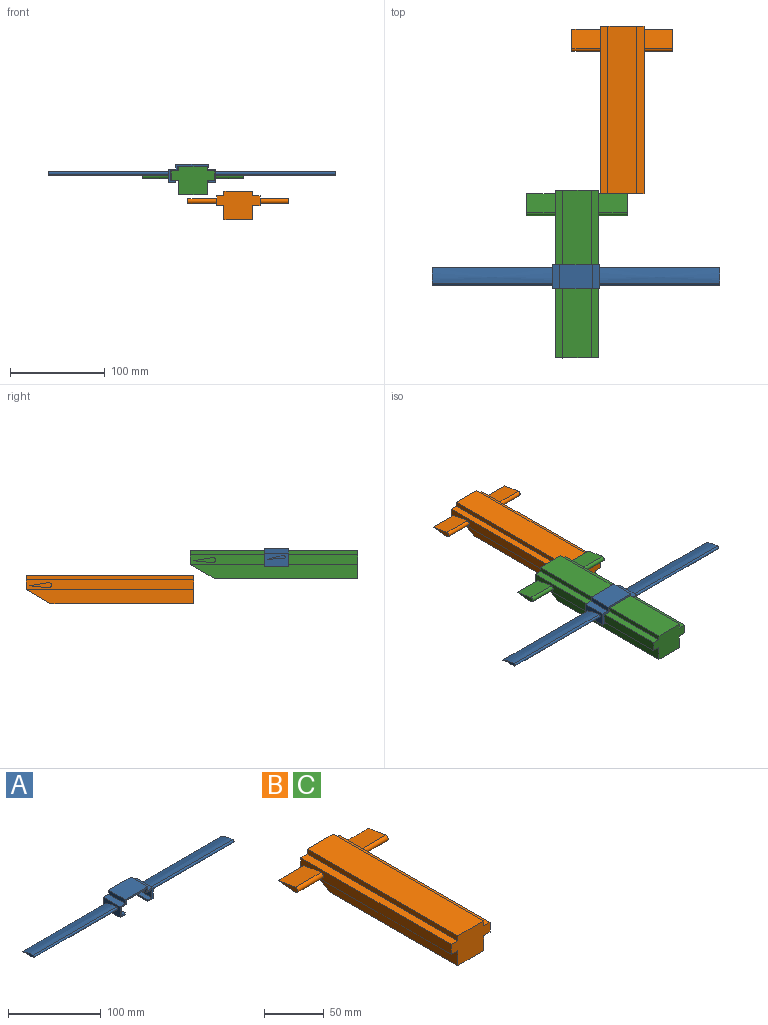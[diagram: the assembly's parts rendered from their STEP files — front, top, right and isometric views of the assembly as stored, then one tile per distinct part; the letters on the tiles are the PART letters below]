
ASSEMBLY  parts=3 mates=1
PART A: 30 faces, bbox 304.1x25.4x19.5 mm
  f0: plane 25.4x5.08mm, normal (1,0,0), area 129mm2, adj f1,f19,f20,f21
  f1: plane 30.48x25.4mm, normal (0,0,-1), area 774.2mm2, adj f0,f2,f20,f21
  f2: plane 25.4x5.08mm, normal (-1,0,0), area 129mm2, adj f1,f3,f20,f21
  f3: plane 25.4x7.62mm, normal (0,0,-1), area 193.5mm2, adj f2,f4,f20,f21
  f4: plane 25.4x10.16mm, normal (-1,0,0), area 258.1mm2, adj f3,f5,f20,f21
  f5: plane 25.4x5.76mm, normal (0,0,1), area 146.3mm2, adj f4,f6,f20,f21
  f6: plane 25.4x2.17mm, normal (-1,0,0), area 55.1mm2, adj f5,f7,f20,f21
  f7: plane 25.4x7.96mm, normal (0,0,-1), area 202.1mm2, adj f6,f8,f20,f21
  f8: plane 25.4x14.25mm, normal (1,0,0), area 325.4mm2, adj f7,f9,f20,f21,f26,f27,f28
  f9: plane 25.4x7.96mm, normal (0,0,1), area 202.1mm2, adj f8,f10,f20,f21
  f10: plane 25.4x5.24mm, normal (1,0,0), area 133.2mm2, adj f9,f11,f20,f21
  f11: plane 34.2x25.4mm, normal (0,0,1), area 868.6mm2, adj f10,f12,f20,f21
  f12: plane 25.4x5.24mm, normal (-1,0,0), area 133.2mm2, adj f11,f13,f20,f21
  f13: plane 25.4x7.96mm, normal (0,0,1), area 202.1mm2, adj f12,f14,f20,f21
  f14: plane 25.4x14.25mm, normal (-1,0,0), area 325.4mm2, adj f13,f15,f20,f21,f22,f23,f24
  f15: plane 25.4x7.96mm, normal (0,0,-1), area 202.1mm2, adj f14,f16,f20,f21
  f16: plane 25.4x2.17mm, normal (1,0,0), area 55.1mm2, adj f15,f17,f20,f21
  f17: plane 25.4x5.76mm, normal (0,0,1), area 146.3mm2, adj f16,f18,f20,f21
  f18: plane 25.4x10.16mm, normal (1,0,0), area 258.1mm2, adj f17,f19,f20,f21
  f19: plane 25.4x7.62mm, normal (0,0,-1), area 193.5mm2, adj f0,f18,f20,f21
  f20: plane 50.11x19.5mm, normal (0,-1,0), area 200mm2, adj f0,f1,f2,f3,f4,f5,f6,f7
  f21: plane 50.11x19.5mm, normal (0,1,0), area 200mm2, adj f0,f1,f2,f3,f4,f5,f6,f7
  f22: extruded ~127x16.9mm, area 2152.8mm2, adj f14,f23,f24,f25
  f23: cylinder r=1.63mm len=127mm, axis (1,0,0), area 650.7mm2, adj f14,f22,f24,f25
  f24: extruded ~127x16.9mm, area 2219.9mm2, adj f14,f22,f23,f25
  f25: plane 18.53x3.99mm, normal (-1,0,0), area 36.6mm2, adj f22,f23,f24
  f26: extruded ~127x16.9mm, area 2152.8mm2, adj f8,f27,f28,f29
  f27: cylinder r=1.63mm len=127mm, axis (-1,0,0), area 650.7mm2, adj f8,f26,f28,f29
  f28: extruded ~127x16.9mm, area 2219.9mm2, adj f8,f26,f27,f29
  f29: plane 18.53x3.99mm, normal (1,0,0), area 36.6mm2, adj f26,f27,f28
PART B: 23 faces, bbox 106.7x177.3x30.5 mm
  f0: plane 177.29x7.62mm, normal (0,0,1), area 1351mm2, adj f1,f11,f12,f13
  f1: plane 177.29x5.08mm, normal (1,0,0), area 900.6mm2, adj f0,f2,f12,f13
  f2: plane 177.29x30.48mm, normal (0,0,1), area 5403.9mm2, adj f1,f3,f12,f13
  f3: plane 177.29x5.08mm, normal (-1,0,0), area 900.6mm2, adj f2,f4,f12,f13
  f4: plane 177.29x7.62mm, normal (0,0,1), area 1351mm2, adj f3,f5,f12,f13
  f5: plane 177.29x10.16mm, normal (-1,0,0), area 1734.3mm2, adj f4,f6,f12,f13,f19,f20,f21
  f6: plane 177.29x7.62mm, normal (0,0,-1), area 1351mm2, adj f5,f7,f12,f13
  f7: plane 177.29x15.24mm, normal (-1,0,0), area 2500.8mm2, adj f6,f8,f12,f14
  f8: plane 150.9x30.48mm, normal (0,0,-1), area 4599.3mm2, adj f7,f9,f12,f14
  f9: plane 177.29x15.24mm, normal (1,0,0), area 2500.8mm2, adj f8,f10,f12,f14
  f10: plane 177.29x7.62mm, normal (0,0,-1), area 1351mm2, adj f9,f11,f12,f13
  f11: plane 177.29x10.16mm, normal (1,0,0), area 1734.3mm2, adj f0,f10,f12,f13,f16,f17,f18
  f12: plane 45.72x30.48mm, normal (0,-1,0), area 1083.9mm2, adj f0,f1,f2,f3,f4,f5,f6,f7
  f13: plane 45.72x15.24mm, normal (0,1,0), area 619.4mm2, adj f0,f1,f2,f3,f4,f5,f6,f10
  f14: plane 30.48x26.4mm, normal (0,0.5,-0.87), area 929mm2, adj f7,f8,f9,f13
  f15: plane 23.12x5.43mm, normal (1,0,0), area 67mm2, adj f16,f17,f18
  f16: plane 30.48x20.41mm, normal (0,0.1,-1), area 625.1mm2, adj f11,f15,f17,f18
  f17: cylinder r=2.72mm len=30.48mm, axis (-1,0,0), area 260.1mm2, adj f11,f15,f16,f18
  f18: plane 30.48x20.41mm, normal (0,0.16,0.99), area 630.6mm2, adj f11,f15,f16,f17
  f19: plane 30.48x20.41mm, normal (0,0.16,0.99), area 630.6mm2, adj f5,f20,f21,f22
  f20: cylinder r=2.72mm len=30.48mm, axis (-1,0,0), area 260.1mm2, adj f5,f19,f21,f22
  f21: plane 30.48x20.41mm, normal (0,0.1,-1), area 625.1mm2, adj f5,f19,f20,f22
  f22: plane 23.12x5.43mm, normal (-1,0,0), area 67mm2, adj f19,f20,f21
PART C: same geometry as B
PLACE A t=(-49.01,-176.28,38.54)mm
PLACE B at identity
PLACE C rot(axis=(-0.2,0.83,0.52),0deg) t=(-47.98,-173.58,26.44)mm
MATE slider C.f11 <-> A.f4  axis (1,0,0) through (-25.12,-176.28,31.54)mm
